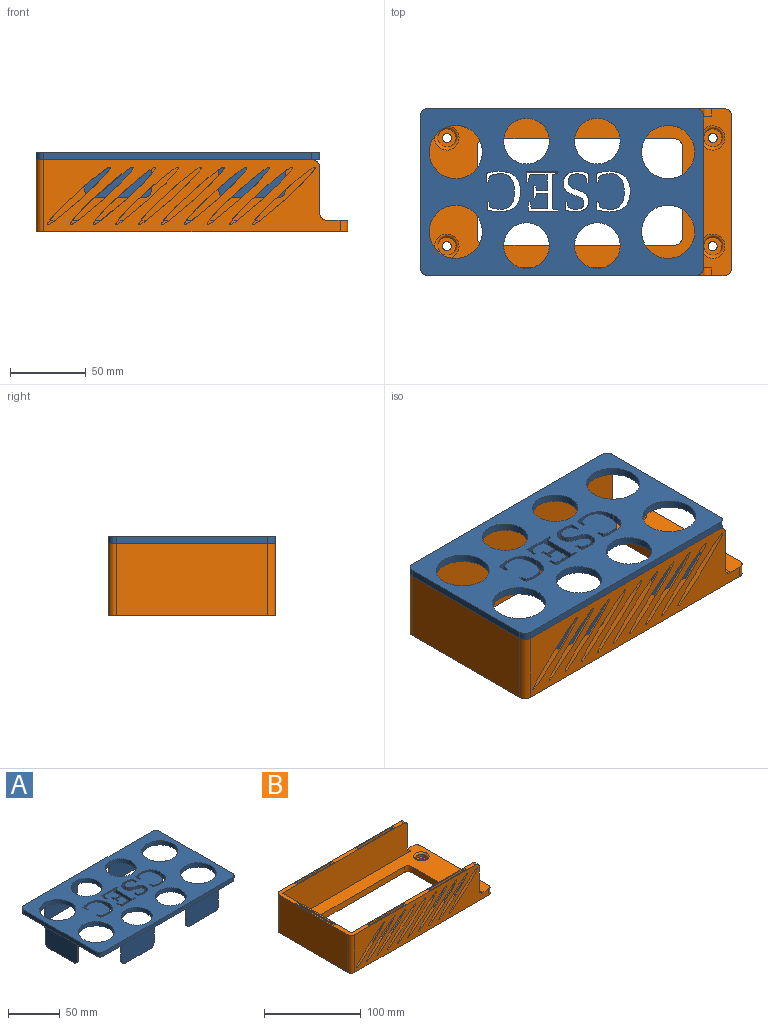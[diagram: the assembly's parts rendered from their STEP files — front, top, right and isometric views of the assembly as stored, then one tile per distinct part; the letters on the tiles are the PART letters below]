
ASSEMBLY  parts=2 mates=1
PART A: 165 faces, bbox 186.5x110x30 mm
  f0: plane 186.5x110mm, normal (0,0,-1), area 12743.1mm2, adj f2,f3,f4,f5,f7,f9,f11,f13
  f1: plane 186.5x110mm, normal (0,0,1), area 13148.1mm2, adj f2,f3,f4,f5,f31,f32,f33,f34
  f2: plane 176.5x5mm, normal (0,1,0), area 882.5mm2, adj f0,f1,f32,f33
  f3: plane 100x5mm, normal (-1,0,0), area 500mm2, adj f0,f1,f33,f34
  f4: plane 176.5x5mm, normal (0,-1,0), area 882.5mm2, adj f0,f1,f31,f34
  f5: plane 100x5mm, normal (1,0,0), area 500mm2, adj f0,f1,f31,f32
  f6: plane 15x1.5mm, normal (-1,0,0), area 22.5mm2, adj f7,f9,f52,f54
  f7: plane 54x25mm, normal (0,1,0), area 1100mm2, adj f0,f6,f8,f10,f51,f52,f53,f54
  f8: plane 15x1.5mm, normal (1,0,0), area 22.5mm2, adj f7,f9,f51,f53
  f9: plane 54x25mm, normal (0,-1,0), area 1100mm2, adj f0,f6,f8,f10,f51,f52,f53,f54
  f10: plane 34x1.5mm, normal (0,0,-1), area 51mm2, adj f7,f9,f53,f54
  f11: plane 54x25mm, normal (0,-1,0), area 1100mm2, adj f0,f12,f14,f15,f47,f48,f49,f50
  f12: plane 15x1.5mm, normal (-1,0,0), area 22.5mm2, adj f11,f13,f47,f49
  f13: plane 54x25mm, normal (0,1,0), area 1100mm2, adj f0,f12,f14,f15,f47,f48,f49,f50
  f14: plane 15x1.5mm, normal (1,0,0), area 22.5mm2, adj f11,f13,f48,f50
  f15: plane 34x1.5mm, normal (0,0,-1), area 51mm2, adj f11,f13,f49,f50
  f16: plane 54x25mm, normal (0,-1,0), area 1100mm2, adj f0,f17,f19,f20,f39,f40,f41,f42
  f17: plane 15x1.5mm, normal (-1,0,0), area 22.5mm2, adj f16,f18,f39,f41
  f18: plane 54x25mm, normal (0,1,0), area 1100mm2, adj f0,f17,f19,f20,f39,f40,f41,f42
  f19: plane 15x1.5mm, normal (1,0,0), area 22.5mm2, adj f16,f18,f40,f42
  f20: plane 34x1.5mm, normal (0,0,-1), area 51mm2, adj f16,f18,f41,f42
  f21: plane 54x25mm, normal (0,-1,0), area 1100mm2, adj f0,f22,f24,f25,f35,f36,f37,f38
  f22: plane 15x1.5mm, normal (-1,0,0), area 22.5mm2, adj f21,f23,f35,f37
  f23: plane 54x25mm, normal (0,1,0), area 1100mm2, adj f0,f22,f24,f25,f35,f36,f37,f38
  f24: plane 15x1.5mm, normal (1,0,0), area 22.5mm2, adj f21,f23,f36,f38
  f25: plane 34x1.5mm, normal (0,0,-1), area 51mm2, adj f21,f23,f37,f38
  f26: plane 15x1.5mm, normal (0,-1,0), area 22.5mm2, adj f27,f29,f44,f46
  f27: plane 54x25mm, normal (-1,0,0), area 1100mm2, adj f0,f26,f28,f30,f43,f44,f45,f46
  f28: plane 15x1.5mm, normal (0,1,0), area 22.5mm2, adj f27,f29,f43,f45
  f29: plane 54x25mm, normal (1,0,0), area 1100mm2, adj f0,f26,f28,f30,f43,f44,f45,f46
  f30: plane 34x1.5mm, normal (0,0,-1), area 51mm2, adj f27,f29,f45,f46
  f31: cylinder r=5mm len=5mm, axis (0,0,-1), area 39.3mm2, adj f0,f1,f4,f5
  f32: cylinder r=5mm len=5mm, axis (0,0,1), area 39.3mm2, adj f0,f1,f2,f5
  f33: cylinder r=5mm len=5mm, axis (0,0,-1), area 39.3mm2, adj f0,f1,f2,f3
  f34: cylinder r=5mm len=5mm, axis (0,0,1), area 39.3mm2, adj f0,f1,f3,f4
  f35: cylinder r=5mm len=5mm, axis (0,-1,0), area 11.8mm2, adj f0,f21,f22,f23
  f36: cylinder r=5mm len=5mm, axis (0,1,0), area 11.8mm2, adj f0,f21,f23,f24
  f37: cylinder r=5mm len=5mm, axis (0,-1,0), area 11.8mm2, adj f21,f22,f23,f25
  f38: cylinder r=5mm len=5mm, axis (0,1,0), area 11.8mm2, adj f21,f23,f24,f25
  f39: cylinder r=5mm len=5mm, axis (0,-1,0), area 11.8mm2, adj f0,f16,f17,f18
  f40: cylinder r=5mm len=5mm, axis (0,1,0), area 11.8mm2, adj f0,f16,f18,f19
  f41: cylinder r=5mm len=5mm, axis (0,-1,0), area 11.8mm2, adj f16,f17,f18,f20
  f42: cylinder r=5mm len=5mm, axis (0,1,0), area 11.8mm2, adj f16,f18,f19,f20
  f43: cylinder r=5mm len=5mm, axis (-1,0,0), area 11.8mm2, adj f0,f27,f28,f29
  f44: cylinder r=5mm len=5mm, axis (1,0,0), area 11.8mm2, adj f0,f26,f27,f29
  f45: cylinder r=5mm len=5mm, axis (-1,0,0), area 11.8mm2, adj f27,f28,f29,f30
  f46: cylinder r=5mm len=5mm, axis (1,0,0), area 11.8mm2, adj f26,f27,f29,f30
  f47: cylinder r=5mm len=5mm, axis (0,-1,0), area 11.8mm2, adj f0,f11,f12,f13
  f48: cylinder r=5mm len=5mm, axis (0,1,0), area 11.8mm2, adj f0,f11,f13,f14
  f49: cylinder r=5mm len=5mm, axis (0,-1,0), area 11.8mm2, adj f11,f12,f13,f15
  f50: cylinder r=5mm len=5mm, axis (0,1,0), area 11.8mm2, adj f11,f13,f14,f15
  f51: cylinder r=5mm len=5mm, axis (0,1,0), area 11.8mm2, adj f0,f7,f8,f9
  f52: cylinder r=5mm len=5mm, axis (0,-1,0), area 11.8mm2, adj f0,f6,f7,f9
  f53: cylinder r=5mm len=5mm, axis (0,1,0), area 11.8mm2, adj f7,f8,f9,f10
  f54: cylinder r=5mm len=5mm, axis (0,-1,0), area 11.8mm2, adj f6,f7,f9,f10
  f55: plane 6.06x5mm, normal (1,-0.02,0), area 30.3mm2, adj f0,f1,f56,f72
  f56: plane 5x1.25mm, normal (0,1,0), area 6.2mm2, adj f0,f1,f55,f57
  f57: plane 5x3.85mm, normal (-0.98,0.18,0), area 19.6mm2, adj f0,f1,f56,f58
  f58: extruded ~5x3.08mm, area 17.1mm2, adj f0,f1,f57,f59
  f59: extruded ~5x4.14mm, area 20.9mm2, adj f0,f1,f58,f60
  f60: extruded ~6.91x5mm, area 39mm2, adj f0,f1,f59,f61
  f61: extruded ~8.58x5mm, area 45.4mm2, adj f0,f1,f60,f62
  f62: extruded ~9.01x5mm, area 47.3mm2, adj f0,f1,f61,f63
  f63: extruded ~7.21x5mm, area 40.3mm2, adj f0,f1,f62,f64
  f64: extruded ~5x3.63mm, area 18.3mm2, adj f0,f1,f63,f65
  f65: extruded ~5x3.13mm, area 17mm2, adj f0,f1,f64,f66
  f66: plane 5x3.34mm, normal (-0.99,-0.17,0), area 17mm2, adj f0,f1,f65,f67
  f67: plane 5x1.27mm, normal (0,-1,0), area 6.3mm2, adj f0,f1,f66,f68
  f68: plane 5.63x5mm, normal (1,0.02,0), area 28.2mm2, adj f0,f1,f67,f69
  f69: extruded ~8.64x5mm, area 43.5mm2, adj f0,f1,f68,f70
  f70: extruded ~9.98x5mm, area 54.2mm2, adj f0,f1,f69,f71
  f71: extruded ~10.07x5mm, area 54.5mm2, adj f0,f1,f70,f73
  f72: extruded ~9.1x5mm, area 46mm2, adj f0,f1,f55,f74
  f73: extruded ~9.57x5mm, area 52.4mm2, adj f0,f1,f71,f74
  f74: extruded ~9.77x5mm, area 53.1mm2, adj f0,f1,f72,f73
  f75: plane 20.61x5mm, normal (0,-1,0), area 103mm2, adj f0,f1,f76,f98
  f76: plane 6.81x5mm, normal (1,-0.05,0), area 34.1mm2, adj f0,f1,f75,f77
  f77: plane 5x1.27mm, normal (0,1,0), area 6.4mm2, adj f0,f1,f76,f78
  f78: plane 5x4.77mm, normal (-0.97,0.22,0), area 24.5mm2, adj f0,f1,f77,f79
  f79: extruded ~6.5x5mm, area 32.6mm2, adj f0,f1,f78,f80
  f80: plane 5.08x5mm, normal (0,1,0), area 25.4mm2, adj f0,f1,f79,f81
  f81: plane 10.53x5mm, normal (1,0,0), area 52.6mm2, adj f0,f1,f80,f82
  f82: plane 6.96x5mm, normal (0,-1,0), area 34.8mm2, adj f0,f1,f81,f83
  f83: plane 5x3.12mm, normal (-0.98,-0.19,0), area 15.9mm2, adj f0,f1,f82,f84
  f84: plane 5x1.23mm, normal (0,-1,0), area 6.2mm2, adj f0,f1,f83,f85
  f85: plane 7.93x5mm, normal (1,0,0), area 39.6mm2, adj f0,f1,f84,f86
  f86: plane 5x1.23mm, normal (0,1,0), area 6.2mm2, adj f0,f1,f85,f87
  f87: plane 5x3.08mm, normal (-0.98,0.19,0), area 15.7mm2, adj f0,f1,f86,f88
  f88: plane 6.96x5mm, normal (0,1,0), area 34.8mm2, adj f0,f1,f87,f89
  f89: plane 10.08x5mm, normal (1,0,0), area 50.4mm2, adj f0,f1,f88,f90
  f90: plane 5x4.21mm, normal (0,-1,0), area 21.1mm2, adj f0,f1,f89,f91
  f91: extruded ~6.24x5mm, area 31.2mm2, adj f0,f1,f90,f92
  f92: plane 5x4.17mm, normal (-0.99,-0.15,0), area 21.1mm2, adj f0,f1,f91,f93
  f93: plane 5x1.27mm, normal (0,-1,0), area 6.3mm2, adj f0,f1,f92,f94
  f94: plane 6.18x5mm, normal (1,0,0), area 30.9mm2, adj f0,f1,f93,f95
  f95: plane 19.36x5mm, normal (0,1,0), area 96.8mm2, adj f0,f1,f94,f96
  f96: plane 5x1.02mm, normal (-1,0,0), area 5.1mm2, adj f0,f1,f95,f97
  f97: plane 5x3.31mm, normal (-0.15,-0.99,0), area 16.7mm2, adj f0,f1,f96,f99
  f98: plane 5x1.02mm, normal (-1,0,0), area 5.1mm2, adj f0,f1,f75,f100
  f99: plane 22.74x5mm, normal (-1,0,0), area 113.7mm2, adj f0,f1,f97,f100
  f100: plane 5x3.31mm, normal (-0.15,0.99,0), area 16.8mm2, adj f0,f1,f98,f99
  f101: extruded ~5x3.73mm, area 19.4mm2, adj f0,f1,f102,f134
  f102: extruded ~5x4.18mm, area 21mm2, adj f0,f1,f101,f103
  f103: extruded ~6.6x5mm, area 35.3mm2, adj f0,f1,f102,f104
  f104: extruded ~5.78x5mm, area 32.1mm2, adj f0,f1,f103,f105
  f105: extruded ~5x3.11mm, area 15.9mm2, adj f0,f1,f104,f106
  f106: extruded ~5x2.14mm, area 13.3mm2, adj f0,f1,f105,f107
  f107: extruded ~5x2.17mm, area 13.1mm2, adj f0,f1,f106,f108
  f108: extruded ~5x2.5mm, area 13.5mm2, adj f0,f1,f107,f109
  f109: extruded ~5x2.5mm, area 13.3mm2, adj f0,f1,f108,f110
  f110: extruded ~5x2.17mm, area 12mm2, adj f0,f1,f109,f111
  f111: extruded ~5x1.54mm, area 10.5mm2, adj f0,f1,f110,f112
  f112: extruded ~5x2.07mm, area 11mm2, adj f0,f1,f111,f113
  f113: extruded ~5x2.9mm, area 16.9mm2, adj f0,f1,f112,f114
  f114: extruded ~5x4.03mm, area 21.2mm2, adj f0,f1,f113,f115
  f115: extruded ~5x4.85mm, area 25.7mm2, adj f0,f1,f114,f116
  f116: plane 5x3.16mm, normal (-0.98,-0.21,0), area 16.2mm2, adj f0,f1,f115,f117
  f117: plane 5x1.25mm, normal (0,-1,0), area 6.2mm2, adj f0,f1,f116,f118
  f118: plane 5.37x5mm, normal (1,0,0), area 26.8mm2, adj f0,f1,f117,f119
  f119: extruded ~6.77x5mm, area 34.2mm2, adj f0,f1,f118,f120
  f120: extruded ~6.41x5mm, area 33.8mm2, adj f0,f1,f119,f121
  f121: extruded ~5x4.83mm, area 27.8mm2, adj f0,f1,f120,f122
  f122: extruded ~5x3.01mm, area 15.5mm2, adj f0,f1,f121,f123
  f123: extruded ~5x2.05mm, area 12.9mm2, adj f0,f1,f122,f124
  f124: extruded ~5x2.16mm, area 12.8mm2, adj f0,f1,f123,f125
  f125: extruded ~5x2.49mm, area 13.4mm2, adj f0,f1,f124,f126
  f126: extruded ~5x2.49mm, area 13.2mm2, adj f0,f1,f125,f127
  f127: extruded ~5x2.16mm, area 12.1mm2, adj f0,f1,f126,f128
  f128: extruded ~5x1.54mm, area 10.9mm2, adj f0,f1,f127,f129
  f129: extruded ~5x2.29mm, area 12mm2, adj f0,f1,f128,f130
  f130: extruded ~5x3.8mm, area 21.1mm2, adj f0,f1,f129,f131
  f131: extruded ~5x4.21mm, area 22.6mm2, adj f0,f1,f130,f132
  f132: extruded ~5x3.43mm, area 17.6mm2, adj f0,f1,f131,f133
  f133: extruded ~5x2.45mm, area 14.8mm2, adj f0,f1,f132,f135
  f134: plane 5.97x5mm, normal (-1,0,0), area 29.8mm2, adj f0,f1,f101,f136
  f135: plane 5x3.48mm, normal (0.98,0.19,0), area 17.7mm2, adj f0,f1,f133,f136
  f136: plane 5x1.26mm, normal (0,1,0), area 6.3mm2, adj f0,f1,f134,f135
  f137: plane 6.06x5mm, normal (1,-0.02,0), area 30.3mm2, adj f0,f1,f138,f154
  f138: plane 5x1.25mm, normal (0,1,0), area 6.2mm2, adj f0,f1,f137,f139
  f139: plane 5x3.85mm, normal (-0.98,0.18,0), area 19.6mm2, adj f0,f1,f138,f140
  f140: extruded ~5x3.08mm, area 17.1mm2, adj f0,f1,f139,f141
  f141: extruded ~5x4.14mm, area 20.9mm2, adj f0,f1,f140,f142
  f142: extruded ~6.91x5mm, area 39mm2, adj f0,f1,f141,f143
  f143: extruded ~8.58x5mm, area 45.4mm2, adj f0,f1,f142,f144
  f144: extruded ~9.01x5mm, area 47.3mm2, adj f0,f1,f143,f145
  f145: extruded ~7.21x5mm, area 40.3mm2, adj f0,f1,f144,f146
  f146: extruded ~5x3.63mm, area 18.3mm2, adj f0,f1,f145,f147
  f147: extruded ~5x3.13mm, area 17mm2, adj f0,f1,f146,f148
  f148: plane 5x3.34mm, normal (-0.99,-0.17,0), area 17mm2, adj f0,f1,f147,f149
  f149: plane 5x1.27mm, normal (0,-1,0), area 6.3mm2, adj f0,f1,f148,f150
  f150: plane 5.63x5mm, normal (1,0.02,0), area 28.2mm2, adj f0,f1,f149,f151
  f151: extruded ~8.64x5mm, area 43.5mm2, adj f0,f1,f150,f152
  f152: extruded ~9.98x5mm, area 54.2mm2, adj f0,f1,f151,f153
  f153: extruded ~10.07x5mm, area 54.5mm2, adj f0,f1,f152,f155
  f154: extruded ~9.1x5mm, area 46mm2, adj f0,f1,f137,f156
  f155: extruded ~9.57x5mm, area 52.4mm2, adj f0,f1,f153,f156
  f156: extruded ~9.77x5mm, area 53.1mm2, adj f0,f1,f154,f155
  f157: cylinder r=17.5mm len=35mm, axis (0,0,1), area 549.8mm2, adj f0,f1
  f158: cylinder r=15mm len=30mm, axis (0,0,1), area 471.2mm2, adj f0,f1
  f159: cylinder r=17.5mm len=35mm, axis (0,0,1), area 549.8mm2, adj f0,f1
  f160: cylinder r=17.5mm len=35mm, axis (0,0,1), area 549.8mm2, adj f0,f1
  f161: cylinder r=15mm len=30mm, axis (0,0,1), area 471.2mm2, adj f0,f1
  f162: cylinder r=17.5mm len=35mm, axis (0,0,1), area 549.8mm2, adj f0,f1
  f163: cylinder r=15mm len=30mm, axis (0,0,1), area 471.2mm2, adj f0,f1
  f164: cylinder r=15mm len=30mm, axis (0,0,1), area 471.2mm2, adj f0,f1
PART B: 118 faces, bbox 205x110x47.5 mm
  f0: plane 186.5x40mm, normal (0,1,0), area 5139.9mm2, adj f10,f11,f17,f18,f21,f23,f67,f69
  f1: plane 55x25mm, normal (0,1,0), area 690.7mm2, adj f3,f4,f10,f29,f30,f63,f64,f65
  f2: plane 55x25mm, normal (0,-1,0), area 690.7mm2, adj f3,f4,f10,f29,f30,f63,f64,f65
  f3: plane 7.63x2.5mm, normal (0,0,1), area 19.1mm2, adj f1,f2,f81,f83
  f4: plane 2.5x1.78mm, normal (0,0,1), area 4.5mm2, adj f1,f2,f65,f81
  f5: plane 55x25mm, normal (0,1,0), area 702.4mm2, adj f7,f8,f9,f10,f31,f32,f60,f61
  f6: plane 55x25mm, normal (0,-1,0), area 702.4mm2, adj f7,f8,f9,f10,f31,f32,f60,f61
  f7: plane 8.08x2.5mm, normal (1,0,0), area 20.2mm2, adj f5,f6,f69,f77
  f8: plane 7.63x2.5mm, normal (0,0,1), area 19.1mm2, adj f5,f6,f73,f75
  f9: plane 3.53x2.5mm, normal (0,0,1), area 8.8mm2, adj f5,f6,f62,f73
  f10: plane 181.5x110mm, normal (0,0,1), area 1616.8mm2, adj f0,f1,f2,f5,f6,f12,f13,f14
  f11: plane 200x110mm, normal (0,0,1), area 9891.5mm2, adj f0,f12,f14,f15,f18,f19,f21,f22
  f12: plane 195x47.5mm, normal (0,1,0), area 8722.5mm2, adj f10,f11,f16,f20,f22,f24,f25,f28
  f13: plane 100x47.5mm, normal (-1,0,0), area 4750mm2, adj f10,f16,f25,f26
  f14: plane 195x47.5mm, normal (0,-1,0), area 6536.9mm2, adj f10,f11,f16,f17,f21,f23,f26,f27
  f15: plane 100x7.5mm, normal (1,0,0), area 750mm2, adj f11,f16,f27,f28
  f16: plane 205x110mm, normal (0,0,-1), area 12986.9mm2, adj f12,f13,f14,f15,f25,f26,f27,f28
  f17: plane 30x5mm, normal (1,0,0), area 150mm2, adj f0,f14,f21,f23
  f18: plane 100x40mm, normal (1,0,0), area 4000mm2, adj f0,f10,f11,f19
  f19: plane 186.5x40mm, normal (0,-1,0), area 7260mm2, adj f10,f11,f18,f20,f22,f24
  f20: plane 30x5mm, normal (1,0,0), area 150mm2, adj f12,f19,f22,f24
  f21: cylinder r=5mm len=5mm, axis (0,1,0), area 39.3mm2, adj f0,f11,f14,f17
  f22: cylinder r=5mm len=5mm, axis (0,1,0), area 39.3mm2, adj f11,f12,f19,f20
  f23: cylinder r=5mm len=5mm, axis (0,-1,0), area 39.3mm2, adj f0,f10,f14,f17
  f24: cylinder r=5mm len=5mm, axis (0,-1,0), area 39.3mm2, adj f10,f12,f19,f20
  f25: cylinder r=5mm len=47.5mm, axis (0,0,-1), area 373.1mm2, adj f10,f12,f13,f16
  f26: cylinder r=5mm len=47.5mm, axis (0,0,1), area 373.1mm2, adj f10,f13,f14,f16
  f27: cylinder r=5mm len=7.5mm, axis (0,0,-1), area 58.9mm2, adj f11,f14,f15,f16
  f28: cylinder r=5mm len=7.5mm, axis (0,0,1), area 58.9mm2, adj f11,f12,f15,f16
  f29: plane 2.5x0.82mm, normal (-1,0,0), area 2mm2, adj f1,f2,f63,f83
  f30: plane 12.56x2.5mm, normal (1,0,0), area 31.4mm2, adj f1,f2,f64,f67
  f31: plane 2.5x1.94mm, normal (-1,0,0), area 4.9mm2, adj f5,f6,f60,f75
  f32: plane 2.5x1.94mm, normal (1,0,0), area 4.9mm2, adj f5,f6,f61,f77
  f33: plane 15x2.5mm, normal (0,-1,0), area 37.5mm2, adj f34,f36,f57,f59
  f34: plane 55x25mm, normal (1,0,0), area 1125mm2, adj f10,f33,f35,f37,f56,f57,f58,f59
  f35: plane 15x2.5mm, normal (0,1,0), area 37.5mm2, adj f34,f36,f56,f58
  f36: plane 55x25mm, normal (-1,0,0), area 1125mm2, adj f10,f33,f35,f37,f56,f57,f58,f59
  f37: plane 35x2.5mm, normal (0,0,1), area 87.5mm2, adj f34,f36,f58,f59
  f38: plane 55x25mm, normal (0,-1,0), area 1125mm2, adj f10,f39,f41,f42,f52,f53,f54,f55
  f39: plane 15x2.5mm, normal (1,0,0), area 37.5mm2, adj f38,f40,f52,f54
  f40: plane 55x25mm, normal (0,1,0), area 1125mm2, adj f10,f39,f41,f42,f52,f53,f54,f55
  f41: plane 15x2.5mm, normal (-1,0,0), area 37.5mm2, adj f38,f40,f53,f55
  f42: plane 35x2.5mm, normal (0,0,1), area 87.5mm2, adj f38,f40,f54,f55
  f43: plane 55x25mm, normal (0,-1,0), area 1125mm2, adj f10,f44,f46,f47,f48,f49,f50,f51
  f44: plane 15x2.5mm, normal (1,0,0), area 37.5mm2, adj f43,f45,f48,f50
  f45: plane 55x25mm, normal (0,1,0), area 1125mm2, adj f10,f44,f46,f47,f48,f49,f50,f51
  f46: plane 15x2.5mm, normal (-1,0,0), area 37.5mm2, adj f43,f45,f49,f51
  f47: plane 35x2.5mm, normal (0,0,1), area 87.5mm2, adj f43,f45,f50,f51
  f48: cylinder r=5mm len=5mm, axis (0,1,0), area 19.6mm2, adj f10,f43,f44,f45
  f49: cylinder r=5mm len=5mm, axis (0,-1,0), area 19.6mm2, adj f10,f43,f45,f46
  f50: cylinder r=5mm len=5mm, axis (0,-1,0), area 19.6mm2, adj f43,f44,f45,f47
  f51: cylinder r=5mm len=5mm, axis (0,1,0), area 19.6mm2, adj f43,f45,f46,f47
  f52: cylinder r=5mm len=5mm, axis (0,1,0), area 19.6mm2, adj f10,f38,f39,f40
  f53: cylinder r=5mm len=5mm, axis (0,-1,0), area 19.6mm2, adj f10,f38,f40,f41
  f54: cylinder r=5mm len=5mm, axis (0,-1,0), area 19.6mm2, adj f38,f39,f40,f42
  f55: cylinder r=5mm len=5mm, axis (0,1,0), area 19.6mm2, adj f38,f40,f41,f42
  f56: cylinder r=5mm len=5mm, axis (-1,0,0), area 19.6mm2, adj f10,f34,f35,f36
  f57: cylinder r=5mm len=5mm, axis (1,0,0), area 19.6mm2, adj f10,f33,f34,f36
  f58: cylinder r=5mm len=5mm, axis (1,0,0), area 19.6mm2, adj f34,f35,f36,f37
  f59: cylinder r=5mm len=5mm, axis (-1,0,0), area 19.6mm2, adj f33,f34,f36,f37
  f60: cylinder r=5mm len=5mm, axis (0,-1,0), area 19.6mm2, adj f5,f6,f10,f31
  f61: cylinder r=5mm len=5mm, axis (0,1,0), area 19.6mm2, adj f5,f6,f10,f32
  f62: cylinder r=5mm len=3.01mm, axis (0,-1,0), area 8.1mm2, adj f5,f6,f9,f69
  f63: cylinder r=5mm len=5mm, axis (0,-1,0), area 19.6mm2, adj f1,f2,f10,f29
  f64: cylinder r=5mm len=5mm, axis (0,1,0), area 19.6mm2, adj f1,f2,f10,f30
  f65: cylinder r=5mm len=3.87mm, axis (0,-1,0), area 11.1mm2, adj f1,f2,f4,f67
  f66: plane 4.99x2.59mm, normal (0,-1,0), area 6.5mm2, adj f11,f67
  f67: extruded ~41.13x37.5mm, area 450.7mm2, adj f0,f1,f2,f14,f30,f65,f66
  f68: plane 4.99x2.59mm, normal (0,-1,0), area 6.5mm2, adj f11,f69
  f69: extruded ~41.13x37.5mm, area 441.6mm2, adj f0,f5,f6,f7,f14,f62,f68
  f70: plane 4.99x2.59mm, normal (0,-1,0), area 6.5mm2, adj f11,f71
  f71: extruded ~41.13x37.5mm, area 544.3mm2, adj f0,f14,f70,f86,f87,f88,f89
  f72: plane 4.99x2.59mm, normal (0,-1,0), area 6.5mm2, adj f11,f73
  f73: extruded ~41.13x37.5mm, area 416mm2, adj f0,f5,f6,f8,f9,f14,f72
  f74: plane 4.99x2.59mm, normal (0,-1,0), area 6.5mm2, adj f11,f75
  f75: extruded ~41.13x37.5mm, area 446.3mm2, adj f0,f5,f6,f8,f14,f31,f74,f86
  f76: plane 4.99x2.59mm, normal (0,-1,0), area 6.5mm2, adj f11,f77
  f77: extruded ~41.13x37.5mm, area 535.8mm2, adj f0,f5,f6,f7,f14,f32,f76
  f78: plane 4.99x2.59mm, normal (0,-1,0), area 6.5mm2, adj f11,f79
  f79: extruded ~41.13x37.5mm, area 538.1mm2, adj f0,f14,f78,f90,f91,f92,f93
  f80: plane 4.99x2.59mm, normal (0,-1,0), area 6.5mm2, adj f11,f81
  f81: extruded ~41.13x37.5mm, area 416mm2, adj f0,f1,f2,f3,f4,f14,f80
  f82: plane 4.99x2.59mm, normal (0,-1,0), area 6.5mm2, adj f11,f83
  f83: extruded ~41.13x37.5mm, area 434.5mm2, adj f0,f1,f2,f3,f14,f29,f82,f90
  f84: plane 4.99x2.59mm, normal (0,-1,0), area 6.5mm2, adj f11,f85
  f85: extruded ~41.13x37.5mm, area 566.1mm2, adj f0,f14,f84
  f86: plane 7.63x2.5mm, normal (0,0,1), area 19.1mm2, adj f71,f75,f87,f89
  f87: plane 14.1x13.98mm, normal (0,-1,0), area 76.3mm2, adj f71,f75,f86,f88
  f88: plane 8.08x2.5mm, normal (-1,0,0), area 20.2mm2, adj f71,f75,f87,f89
  f89: plane 14.1x13.98mm, normal (0,1,0), area 76.3mm2, adj f71,f75,f86,f88
  f90: plane 7.63x2.5mm, normal (0,0,1), area 19.1mm2, adj f79,f83,f91,f93
  f91: plane 16x15.85mm, normal (0,-1,0), area 90.8mm2, adj f79,f83,f90,f92
  f92: plane 8.55x2.5mm, normal (-1,0,0), area 21.4mm2, adj f79,f83,f91,f93
  f93: plane 16x15.85mm, normal (0,1,0), area 90.8mm2, adj f79,f83,f90,f92
  f94: cylinder r=3mm len=6mm, axis (0,0,1), area 47.1mm2, adj f16,f105
  f95: cylinder r=3mm len=6mm, axis (0,0,1), area 47.1mm2, adj f16,f103
  f96: cylinder r=3mm len=6mm, axis (0,0,1), area 47.1mm2, adj f16,f101
  f97: cylinder r=3mm len=6mm, axis (0,0,1), area 47.1mm2, adj f16,f99
  f98: cylinder r=6mm len=12mm, axis (0,0,1), area 113.1mm2, adj f99,f106
  f99: plane 12x12mm, normal (0,0,1), area 84.8mm2, adj f97,f98
  f100: cylinder r=6mm len=12mm, axis (0,0,1), area 113.1mm2, adj f101,f107
  f101: plane 12x12mm, normal (0,0,1), area 84.8mm2, adj f96,f100
  f102: cylinder r=6mm len=12mm, axis (0,0,1), area 113.1mm2, adj f103,f108
  f103: plane 12x12mm, normal (0,0,1), area 84.8mm2, adj f95,f102
  f104: cylinder r=6mm len=12mm, axis (0,0,1), area 113.1mm2, adj f105,f109
  f105: plane 12x12mm, normal (0,0,1), area 84.8mm2, adj f94,f104
  f106: torus R=8mm, axis (0,0,1), area 132.8mm2, adj f11,f98
  f107: torus R=8mm, axis (0,0,1), area 132.8mm2, adj f11,f100
  f108: torus R=8mm, axis (0,0,1), area 132.8mm2, adj f11,f102
  f109: torus R=8mm, axis (0,0,1), area 132.8mm2, adj f11,f104
  f110: plane 60x7.5mm, normal (1,0,0), area 450mm2, adj f11,f16,f114,f117
  f111: plane 125x7.5mm, normal (0,1,0), area 937.5mm2, adj f11,f16,f114,f115
  f112: plane 60x7.5mm, normal (-1,0,0), area 450mm2, adj f11,f16,f115,f116
  f113: plane 125x7.5mm, normal (0,-1,0), area 937.5mm2, adj f11,f16,f116,f117
  f114: cylinder r=5mm len=7.5mm, axis (0,0,-1), area 58.9mm2, adj f11,f16,f110,f111
  f115: cylinder r=5mm len=7.5mm, axis (0,0,1), area 58.9mm2, adj f11,f16,f111,f112
  f116: cylinder r=5mm len=7.5mm, axis (0,0,-1), area 58.9mm2, adj f11,f16,f112,f113
  f117: cylinder r=5mm len=7.5mm, axis (0,0,1), area 58.9mm2, adj f11,f16,f110,f113
PLACE A t=(0,0,-5)mm
PLACE B at identity fixed
MATE fastened A.f33 <-> B.f25  axis (0,0,-1) through (-97.5,50,45)mm
